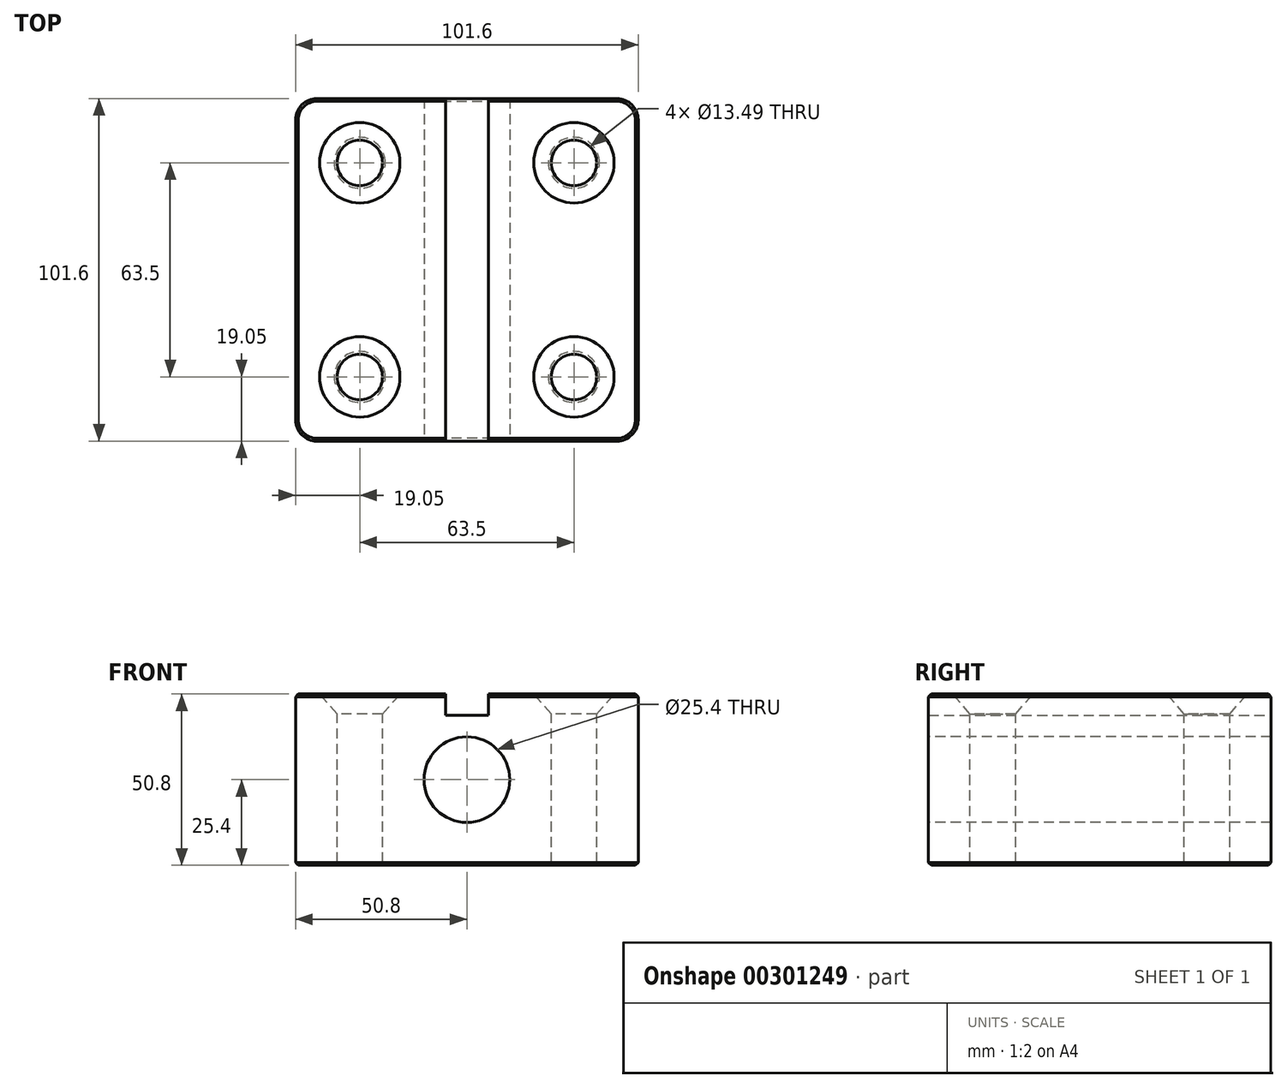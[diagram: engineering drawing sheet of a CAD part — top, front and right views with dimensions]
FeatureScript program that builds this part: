
annotation { "Feature Type Name" : "Feature", "Feature Type Description" : "" }
export const myFeature = defineFeature(function(context is Context, id is Id, definition is map)
    precondition{}
    {
        {
            var Q0;
            Q0=qCreatedBy(makeId("Front.planeOp"),FACE);
            var sketch = newSketch(context, id + "F0", { "sketchPlane" : qUnion([Q0])});
            skLineSegment(sketch, "E0.bottom", {"start": v(-50.8, 25.4) * mm, "end": v(50.8, 25.4) * mm});
            skLineSegment(sketch, "E0.top", {"start": v(-50.8, -25.4) * mm, "end": v(50.8, -25.4) * mm});
            skLineSegment(sketch, "E0.left", {"start": v(-50.8, 25.4) * mm, "end": v(-50.8, -25.4) * mm});
            skLineSegment(sketch, "E0.right", {"start": v(50.8, 25.4) * mm, "end": v(50.8, -25.4) * mm});
            skLineSegment(sketch, "E1.bottom", {"start": v(-6.35, 25.4) * mm, "end": v(6.35, 25.4) * mm});
            skLineSegment(sketch, "E1.top", {"start": v(-6.35, 19.05) * mm, "end": v(6.35, 19.05) * mm});
            skLineSegment(sketch, "E1.left", {"start": v(-6.35, 25.4) * mm, "end": v(-6.35, 19.05) * mm});
            skLineSegment(sketch, "E1.right", {"start": v(6.35, 25.4) * mm, "end": v(6.35, 19.05) * mm});
            skSolve(sketch);
        }
        {
            var Q0;
            Q0=makeQuery(id+"F0.imprint","IMPRINT",FACE,{"disambiguationData":[TD([[makeQuery(id+"F0.imprint","IMPRINT",EDGE,{"derivedFrom":sQuery(id+"F0.wireOp",EDGE,"E0.bottom")}),-1.0]])]});
            extrude(context, id + "F1", {"entities" : qUnion([Q0]), "endBound" : BoundingType.SYMMETRIC, "depth" : 101.6 * mm});
        }
        {
            var Q0;
            Q0=makeQuery(id+"F1.opExtrude","SWEPT_FACE",FACE,{"disambiguationData":[OSD([sQuery(id+"F0.wireOp",EDGE,"E0.bottom")])]});
            var sketch = newSketch(context, id + "F2", { "sketchPlane" : qUnion([Q0])});
            skPoint(sketch, "E2", {"position": v(-31.75, 31.75) * mm});
            skPoint(sketch, "E3.MirrorP", {"position": v(31.75, 31.75) * mm});
            skPoint(sketch, "E4.MirrorP", {"position": v(31.75, -31.75) * mm});
            skPoint(sketch, "E5.MirrorP", {"position": v(-31.75, -31.75) * mm});
            skSolve(sketch);
        }
        {
            var Q0;
            Q0=sQuery(id+"F2.wireOp",VERTEX,"E2");
            var Q1;
            Q1=sQuery(id+"F2.wireOp",VERTEX,"E3.MirrorP");
            var Q2;
            Q2=sQuery(id+"F2.wireOp",VERTEX,"E4.MirrorP");
            var Q3;
            Q3=sQuery(id+"F2.wireOp",VERTEX,"E5.MirrorP");
            var Q4;
            Q4=makeQuery(id+"F1.opExtrude","SWEPT_BODY",BODY,{"disambiguationData":[OSD([sQuery(id+"F0.wireOp",EDGE,"E0.bottom"),sQuery(id+"F0.wireOp",EDGE,"E0.top"),sQuery(id+"F0.wireOp",EDGE,"E0.left"),sQuery(id+"F0.wireOp",EDGE,"E0.right")])]});
            hole(context, id + "F3", {"style" : HoleStyle.C_SINK, "endStyle" : HoleEndStyle.THROUGH, "standardTappedOrClearance" : lookupTablePath({ "standard" : "ANSI", "fit" : "Normal (ASME)", "size" : "1/2", "type" : "Clearance" }), "standardBlindInLast" : lookupTablePath({ "fit" : "Free", "standard" : "ANSI", "size" : "1/2", "type" : "Clearance" }), "holeDiameter" : 13.5 * mm, "cSinkDiameter" : 23.83 * mm, "cSinkAngle" : 82 * degree, "tappedDepth" : 12.7 * mm, "tapClearance" : 3, "locations" : qUnion([Q0, Q1, Q2, Q3]), "scope" : qUnion([Q4])});
        }
        {
            var Q0;
            Q0=makeQuery(id+"F1.opExtrude","CAP_EDGE",EDGE,{"disambiguationData":[OSD([sQuery(id+"F0.wireOp",EDGE,"E0.left")])],"isStart":true});
            var Q1;
            Q1=makeQuery(id+"F1.opExtrude","CAP_EDGE",EDGE,{"disambiguationData":[OSD([sQuery(id+"F0.wireOp",EDGE,"E0.left")])],"isStart":false});
            var Q2;
            Q2=makeQuery(id+"F1.opExtrude","CAP_EDGE",EDGE,{"disambiguationData":[OSD([sQuery(id+"F0.wireOp",EDGE,"E0.right")])],"isStart":false});
            var Q3;
            Q3=makeQuery(id+"F1.opExtrude","CAP_EDGE",EDGE,{"disambiguationData":[OSD([sQuery(id+"F0.wireOp",EDGE,"E0.right")])],"isStart":true});
            fillet(context, id + "F4", {"entities" : qUnion([Q0, Q1, Q2, Q3]), "radius" : 6.35 * mm, "tangentPropagation" : true, "allowEdgeOverflow" : false});
        }
        {
            var Q0;
            Q0=makeQuery(id+"F1.opExtrude","SWEPT_FACE",FACE,{"disambiguationData":[OSD([sQuery(id+"F0.wireOp",EDGE,"E0.top")])]});
            chamfer(context, id + "F5", {"entities" : qUnion([Q0]), "width" : 0.81 * mm, "tangentPropagation" : true});
        }
        {
            var Q0;
            Q0=makeQuery(id+"F1.opExtrude","CAP_EDGE",EDGE,{"disambiguationData":[OSD([sQuery(id+"F0.wireOp",EDGE,"E0.bottom")])],"isStart":true});
            var Q1;
            Q1=makeQuery(id+"F1.opExtrude","SWEPT_EDGE",EDGE,{"disambiguationData":[OSD([sQuery(id+"F0.wireOp",EDGE,"E0.bottom"),sQuery(id+"F0.wireOp",EDGE,"E0.right")])]});
            var Q2;
            Q2=makeQuery(id+"F1.opExtrude","SWEPT_EDGE",EDGE,{"disambiguationData":[OSD([sQuery(id+"F0.wireOp",EDGE,"E0.bottom"),sQuery(id+"F0.wireOp",EDGE,"E0.left")])]});
            var Q3;
            Q3=makeQuery(id+"F1.opExtrude","CAP_EDGE",EDGE,{"disambiguationData":[OSD([sQuery(id+"F0.wireOp",EDGE,"E0.bottom")])],"isStart":false});
            chamfer(context, id + "F6", {"entities" : qUnion([Q0, Q1, Q2, Q3]), "width" : 0.81 * mm, "tangentPropagation" : true});
        }
        {
            var Q0;
            Q0=makeQuery(id+"F1.opExtrude","CAP_FACE",FACE,{"disambiguationData":[OSD([sQuery(id+"F0.wireOp",EDGE,"E0.bottom"),sQuery(id+"F0.wireOp",EDGE,"E0.top"),sQuery(id+"F0.wireOp",EDGE,"E0.left"),sQuery(id+"F0.wireOp",EDGE,"E0.right")])],"isStart":false});
            var sketch = newSketch(context, id + "F7", { "sketchPlane" : qUnion([Q0])});
            skPoint(sketch, "E6", {"position": v(0, 0) * mm});
            skSolve(sketch);
        }
        {
            var Q0;
            Q0=sQuery(id+"F7.wireOp",VERTEX,"E6");
            var Q1;
            Q1=makeQuery(id+"F1.opExtrude","SWEPT_BODY",BODY,{"disambiguationData":[OSD([sQuery(id+"F0.wireOp",EDGE,"E0.bottom"),sQuery(id+"F0.wireOp",EDGE,"E0.top"),sQuery(id+"F0.wireOp",EDGE,"E0.left"),sQuery(id+"F0.wireOp",EDGE,"E0.right")])]});
            hole(context, id + "F8", {"style" : HoleStyle.SIMPLE, "endStyle" : HoleEndStyle.THROUGH, "holeDiameter" : 25.4 * mm, "tappedDepth" : 12.7 * mm, "tapClearance" : 3, "locations" : qUnion([Q0]), "scope" : qUnion([Q1])});
        }
    });
